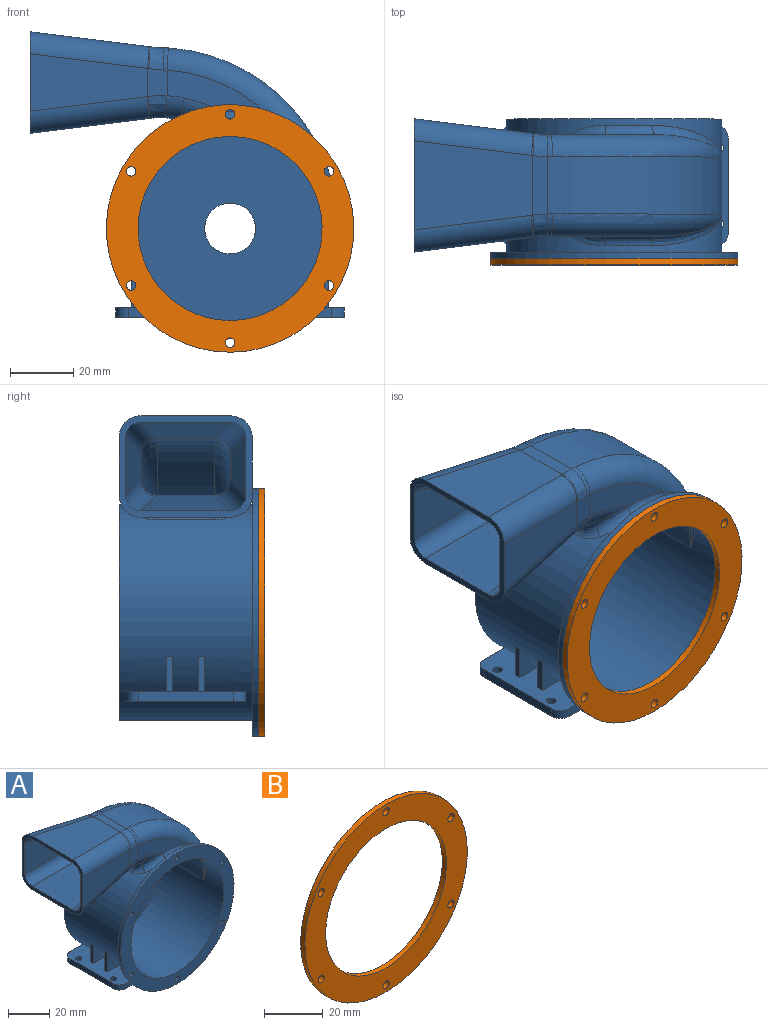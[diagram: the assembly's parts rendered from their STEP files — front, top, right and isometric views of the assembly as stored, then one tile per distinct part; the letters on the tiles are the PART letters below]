
ASSEMBLY  parts=2 mates=1
PART A: 125 faces, bbox 102.7x46.3x101.7 mm
  f0: plane 38x12.96mm, normal (0,0,1), area 439.5mm2, adj f1,f111,f113,f114,f115,f116,f117,f118
  f1: cylinder r=34mm len=68mm, axis (0,1,0), area 6152.7mm2, adj f0,f8,f9,f41,f42,f43,f44,f45
  f2: cylinder r=1.5mm len=3mm, axis (0,-1,0), area 18.8mm2, adj f7,f94
  f3: cylinder r=1.5mm len=3mm, axis (0,-1,0), area 18.8mm2, adj f7,f94
  f4: cylinder r=1.5mm len=3mm, axis (0,-1,0), area 18.8mm2, adj f7,f94
  f5: cylinder r=1.5mm len=3mm, axis (0,-1,0), area 18.8mm2, adj f7,f94
  f6: cylinder r=1.5mm len=3mm, axis (0,-1,0), area 18.8mm2, adj f7,f94
  f7: plane 78x78mm, normal (0,-1,0), area 1519mm2, adj f2,f3,f4,f5,f6,f50,f93,f104
  f8: plane 68x68mm, normal (0,1,0), area 3430.6mm2, adj f1,f92
  f9: cylinder r=57mm len=56.97mm, axis (0,1,0), area 1577.2mm2, adj f1,f18,f24,f25,f39,f40
  f10: plane 32.97x15.29mm, normal (0,1,0), area 215.6mm2, adj f17,f25,f29,f30,f48
  f11: plane 32.97x15.29mm, normal (0,-1,0), area 215.6mm2, adj f19,f34,f35,f40,f42
  f12: plane 42.71x32.71mm, normal (-1,0,0), area 261.9mm2, adj f13,f14,f15,f16,f21,f26,f31,f36
  f13: plane 36.91x18.11mm, normal (0.12,0.99,0), area 502mm2, adj f12,f17,f21,f26
  f14: plane 37.3x28.11mm, normal (0.12,0,-0.99), area 881.4mm2, adj f12,f20,f26,f27,f31,f32
  f15: plane 36.91x18.11mm, normal (0.12,-0.99,0), area 502mm2, adj f12,f19,f31,f36
  f16: plane 37.4x28.11mm, normal (0.12,0,0.99), area 883.1mm2, adj f12,f18,f21,f22,f36,f37
  f17: cylinder r=50mm len=8.88mm, axis (0,0,-1), area 52.4mm2, adj f10,f13,f22,f23,f24,f27,f28
  f18: cylinder r=50mm len=18.76mm, axis (0,1,0), area 83.5mm2, adj f9,f16,f23,f38
  f19: cylinder r=50mm len=8.88mm, axis (0,0,-1), area 52.4mm2, adj f11,f15,f32,f33,f37,f38,f39
  f20: cylinder r=30mm len=18.79mm, axis (0,1,0), area 128.4mm2, adj f14,f28,f29,f33,f34,f45
  f21: cylinder r=7mm len=37.26mm, axis (0.98,-0.12,-0.12), area 408.1mm2, adj f12,f13,f16,f22
  f22: bspline ~7.01x7mm, area 4.9mm2, adj f16,f17,f21,f23
  f23: bspline ~13.94x8.18mm, area 48mm2, adj f17,f18,f22,f24
  f24: bspline ~8.17x7.36mm, area 15.9mm2, adj f9,f17,f23,f25
  f25: torus R=50mm, axis (0,-1,0), area 672mm2, adj f9,f10,f24,f49
  f26: cylinder r=7mm len=37.26mm, axis (-0.98,0.12,-0.12), area 408.1mm2, adj f12,f13,f14,f27
  f27: bspline ~6.99x6.99mm, area 4mm2, adj f14,f17,f26,f28
  f28: bspline ~10.18x7.87mm, area 59mm2, adj f17,f20,f27,f29
  f29: torus R=37mm, axis (0,-1,0), area 46.8mm2, adj f10,f20,f28,f30,f46
  f30: torus R=42mm, axis (0,-1,0), area 37.5mm2, adj f10,f29,f47
  f31: cylinder r=7mm len=37.26mm, axis (0.98,0.12,0.12), area 408.1mm2, adj f12,f14,f15,f32
  f32: bspline ~6.99x6.99mm, area 4mm2, adj f14,f19,f31,f33
  f33: bspline ~10.09x7.45mm, area 59mm2, adj f19,f20,f32,f34
  f34: torus R=37mm, axis (0,-1,0), area 46.8mm2, adj f11,f20,f33,f35,f44
  f35: torus R=42mm, axis (0,-1,0), area 37.5mm2, adj f11,f34,f43
  f36: cylinder r=7mm len=37.26mm, axis (-0.98,-0.12,0.12), area 408.1mm2, adj f12,f15,f16,f37
  f37: bspline ~7.01x7mm, area 4.9mm2, adj f16,f19,f36,f38
  f38: bspline ~13.94x8.18mm, area 48mm2, adj f18,f19,f37,f39
  f39: bspline ~8.17x7.36mm, area 15.9mm2, adj f9,f19,f38,f40
  f40: torus R=50mm, axis (0,-1,0), area 672mm2, adj f9,f11,f39,f41
  f41: bspline ~34.98x22.71mm, area 96.9mm2, adj f1,f40,f42
  f42: torus R=37mm, axis (0,-1,0), area 72.8mm2, adj f1,f11,f41,f43
  f43: bspline ~15.78x9.16mm, area 71.6mm2, adj f1,f35,f42,f44
  f44: bspline ~8.86x8.69mm, area 37.5mm2, adj f1,f34,f43,f45
  f45: cylinder r=3mm len=18mm, axis (0,-1,0), area 134.6mm2, adj f1,f20,f44,f46
  f46: bspline ~8.86x8.69mm, area 37.5mm2, adj f1,f29,f45,f47
  f47: bspline ~15.78x9.16mm, area 71.6mm2, adj f1,f30,f46,f48
  f48: torus R=37mm, axis (0,-1,0), area 72.8mm2, adj f1,f10,f47,f49
  f49: bspline ~34.98x22.71mm, area 96.9mm2, adj f1,f25,f48
  f50: cylinder r=32mm len=64mm, axis (0,1,0), area 6244.5mm2, adj f7,f51,f52,f83,f84,f85,f86,f87
  f51: plane 64x64mm, normal (0,-1,0), area 3015.9mm2, adj f50,f90,f92
  f52: cylinder r=55mm len=54.97mm, axis (0,1,0), area 1521.8mm2, adj f50,f60,f66,f67,f81,f82
  f53: plane 32.97x15.29mm, normal (0,-1,0), area 215.6mm2, adj f59,f67,f71,f72,f90
  f54: plane 32.97x15.29mm, normal (0,1,0), area 215.6mm2, adj f61,f76,f77,f82,f84
  f55: plane 36.66x18.05mm, normal (-0.12,-0.99,0), area 497.4mm2, adj f12,f59,f63,f68
  f56: plane 37.05x28.05mm, normal (-0.12,0,0.99), area 874.3mm2, adj f12,f62,f68,f69,f73,f74
  f57: plane 36.66x18.05mm, normal (-0.12,0.99,0), area 497.4mm2, adj f12,f61,f73,f78
  f58: plane 37.15x28.05mm, normal (-0.12,0,-0.99), area 876.1mm2, adj f12,f60,f63,f64,f78,f79
  f59: cylinder r=52mm len=8.88mm, axis (0,0,-1), area 54.5mm2, adj f53,f55,f64,f65,f66,f69,f70
  f60: cylinder r=52mm len=18.76mm, axis (0,1,0), area 86.8mm2, adj f52,f58,f65,f80
  f61: cylinder r=52mm len=8.88mm, axis (0,0,-1), area 54.5mm2, adj f54,f57,f74,f75,f79,f80,f81
  f62: cylinder r=32mm len=18.79mm, axis (0,1,0), area 137mm2, adj f56,f70,f71,f75,f76,f87
  f63: cylinder r=5mm len=36.91mm, axis (0.98,-0.12,-0.12), area 289.6mm2, adj f12,f55,f58,f64
  f64: bspline ~5.02x5.02mm, area 3.6mm2, adj f58,f59,f63,f65
  f65: bspline ~14.48x6.23mm, area 36.1mm2, adj f59,f60,f64,f66
  f66: bspline ~5.52x5.15mm, area 11.3mm2, adj f52,f59,f65,f67
  f67: torus R=50mm, axis (0,-1,0), area 467.8mm2, adj f52,f53,f66,f91
  f68: cylinder r=5mm len=36.91mm, axis (-0.98,0.12,-0.12), area 289.6mm2, adj f12,f55,f56,f69
  f69: bspline ~5.01x5.01mm, area 2.9mm2, adj f56,f59,f68,f70
  f70: bspline ~7.9x5.47mm, area 45.1mm2, adj f59,f62,f69,f71
  f71: torus R=37mm, axis (0,-1,0), area 34.6mm2, adj f53,f62,f70,f72,f88
  f72: torus R=42mm, axis (0,-1,0), area 27.2mm2, adj f53,f71,f89
  f73: cylinder r=5mm len=36.91mm, axis (0.98,0.12,0.12), area 289.6mm2, adj f12,f56,f57,f74
  f74: bspline ~5.01x5.01mm, area 2.9mm2, adj f56,f61,f73,f75
  f75: bspline ~10.49x5.47mm, area 45.1mm2, adj f61,f62,f74,f76
  f76: torus R=37mm, axis (0,-1,0), area 34.6mm2, adj f54,f62,f75,f77,f86
  f77: torus R=42mm, axis (0,-1,0), area 27.2mm2, adj f54,f76,f85
  f78: cylinder r=5mm len=36.91mm, axis (-0.98,-0.12,0.12), area 289.6mm2, adj f12,f57,f58,f79
  f79: bspline ~5.02x5.02mm, area 3.6mm2, adj f58,f61,f78,f80
  f80: bspline ~14.48x6.23mm, area 36.1mm2, adj f60,f61,f79,f81
  f81: bspline ~7.88x5.36mm, area 11.3mm2, adj f52,f61,f80,f82
  f82: torus R=50mm, axis (0,-1,0), area 467.8mm2, adj f52,f54,f81,f83
  f83: bspline ~35.03x21.37mm, area 152.3mm2, adj f50,f82,f84
  f84: torus R=37mm, axis (0,-1,0), area 117mm2, adj f50,f54,f83,f85
  f85: bspline ~15.47x12.4mm, area 106.8mm2, adj f50,f77,f84,f86
  f86: bspline ~14.76x10.53mm, area 46.4mm2, adj f50,f76,f85,f87
  f87: cylinder r=5mm len=18mm, axis (0,-1,0), area 224.3mm2, adj f50,f62,f86,f88
  f88: bspline ~14.76x10.56mm, area 46.4mm2, adj f50,f71,f87,f89
  f89: bspline ~15.47x12.4mm, area 106.8mm2, adj f50,f72,f88,f90
  f90: torus R=37mm, axis (0,-1,0), area 117mm2, adj f51,f53,f89,f91
  f91: bspline ~35.03x21.37mm, area 152.3mm2, adj f50,f67,f90
  f92: cylinder r=8mm len=16mm, axis (0,-1,0), area 100.5mm2, adj f8,f51
  f93: cylinder r=39mm len=78mm, axis (0,-1,0), area 490.1mm2, adj f7,f94
  f94: plane 78x78mm, normal (0,1,0), area 1104.3mm2, adj f1,f2,f3,f4,f5,f6,f93,f104
  f95: plane 38x16.71mm, normal (0,0,-1), area 614.1mm2, adj f1,f96,f98,f99,f100,f105,f109,f110
  f96: plane 30x3mm, normal (1,0,0), area 90mm2, adj f95,f97,f109,f110
  f97: plane 38x12.96mm, normal (0,0,1), area 439.5mm2, adj f1,f96,f98,f99,f100,f101,f102,f103
  f98: plane 12.71x3mm, normal (0,-1,0), area 32.2mm2, adj f1,f95,f97,f110
  f99: plane 12.71x3mm, normal (0,1,0), area 32.2mm2, adj f1,f95,f97,f109
  f100: cylinder r=1.5mm len=3mm, axis (0,0,1), area 28.3mm2, adj f95,f97
  f101: plane 11.04x7.96mm, normal (0,-1,0), area 37.7mm2, adj f1,f97,f103
  f102: plane 11.04x7.96mm, normal (0,1,0), area 37.7mm2, adj f1,f97,f103
  f103: plane 11.04x2mm, normal (1,0,0), area 22.1mm2, adj f1,f97,f101,f102
  f104: cylinder r=1.5mm len=3mm, axis (0,-1,0), area 18.8mm2, adj f7,f94
  f105: cylinder r=1.5mm len=3mm, axis (0,0,1), area 28.3mm2, adj f95,f97
  f106: plane 11.04x7.96mm, normal (0,-1,0), area 37.7mm2, adj f1,f97,f108
  f107: plane 11.04x7.96mm, normal (0,1,0), area 37.7mm2, adj f1,f97,f108
  f108: plane 11.04x2mm, normal (1,0,0), area 22.1mm2, adj f1,f97,f106,f107
  f109: cylinder r=4mm len=4mm, axis (0,0,1), area 18.8mm2, adj f95,f96,f97,f99
  f110: cylinder r=4mm len=4mm, axis (0,0,-1), area 18.8mm2, adj f95,f96,f97,f98
  f111: plane 30x3mm, normal (-1,0,0), area 90mm2, adj f0,f112,f123,f124
  f112: plane 38x16.71mm, normal (0,0,-1), area 614.1mm2, adj f1,f111,f113,f114,f115,f119,f123,f124
  f113: plane 12.71x3mm, normal (0,-1,0), area 32.2mm2, adj f0,f1,f112,f124
  f114: plane 12.71x3mm, normal (0,1,0), area 32.2mm2, adj f0,f1,f112,f123
  f115: cylinder r=1.5mm len=3mm, axis (0,0,1), area 28.3mm2, adj f0,f112
  f116: plane 11.04x7.96mm, normal (0,1,0), area 37.7mm2, adj f0,f1,f118
  f117: plane 11.04x7.96mm, normal (0,-1,0), area 37.7mm2, adj f0,f1,f118
  f118: plane 11.04x2mm, normal (-1,0,0), area 22.1mm2, adj f0,f1,f116,f117
  f119: cylinder r=1.5mm len=3mm, axis (0,0,1), area 28.3mm2, adj f0,f112
  f120: plane 11.04x7.96mm, normal (0,1,0), area 37.7mm2, adj f0,f1,f122
  f121: plane 11.04x7.96mm, normal (0,-1,0), area 37.7mm2, adj f0,f1,f122
  f122: plane 11.04x2mm, normal (-1,0,0), area 22.1mm2, adj f0,f1,f120,f121
  f123: cylinder r=4mm len=4mm, axis (0,0,-1), area 18.8mm2, adj f0,f111,f112,f114
  f124: cylinder r=4mm len=4mm, axis (0,0,1), area 18.8mm2, adj f0,f111,f112,f113
PART B: 10 faces, bbox 78x2x78 mm
  f0: cylinder r=1.5mm len=3mm, axis (0,-1,0), area 18.8mm2, adj f7,f8
  f1: cylinder r=1.5mm len=3mm, axis (0,-1,0), area 18.8mm2, adj f7,f8
  f2: cylinder r=1.5mm len=3mm, axis (0,-1,0), area 18.8mm2, adj f7,f8
  f3: cylinder r=1.5mm len=3mm, axis (0,-1,0), area 18.8mm2, adj f7,f8
  f4: cylinder r=1.5mm len=3mm, axis (0,-1,0), area 18.8mm2, adj f7,f8
  f5: cylinder r=29mm len=58mm, axis (0,1,0), area 364.4mm2, adj f7,f8
  f6: cylinder r=39mm len=78mm, axis (0,1,0), area 490.1mm2, adj f7,f8
  f7: plane 78x78mm, normal (0,-1,0), area 2093.9mm2, adj f0,f1,f2,f3,f4,f5,f6,f9
  f8: plane 78x78mm, normal (0,1,0), area 2093.9mm2, adj f0,f1,f2,f3,f4,f5,f6,f9
  f9: cylinder r=1.5mm len=3mm, axis (0,-1,0), area 18.8mm2, adj f7,f8
PLACE A at identity
PLACE B t=(0,-23,0)mm
MATE fastened B.f4 <-> A.f6  axis (0,1,0) through (0,-23,36)mm
